# Revit family: TD92_OND757_MAR030_RVT20_R00
name_source: partatom
category: Mobiliário
units: mm (PartAtom-declared; Revit-internal decimal feet)

## family parameters
Com base no plano de trabalho = Não
Compartilhado = Não
Corte com vazios quando carregada = Não
Número OmniClass = 23.40.20.00
Ponto de cálculo do ambiente = Não
Sempre na vertical = Sim
Título OmniClass = General Furniture and Specialties

## types (1)
- TD92_OND757_MAR030_RVT20_R00
    Descrição = É impossível não se apaixonar pelos detalhes leves e pela beleza do Cabide Tramontina Onda em Polietileno. Um produto que dará um toque a mais na sua decoração com muita facilidade e permitirá que o ambiente, fique ainda mais encantador.
    Elevação padrão = 0  [stored 0 ft]
    Fabricante = Tramontina Delta S/A
    Modelo = Cabide Tramontina Onda em Polietileno Mariner
    Nota-chave = 92757030
    URL = https://www.tramontinastore.com

note: [stored X ft] marks values corroborated as IEEE doubles in the binary element streams (Revit-internal decimal feet)
